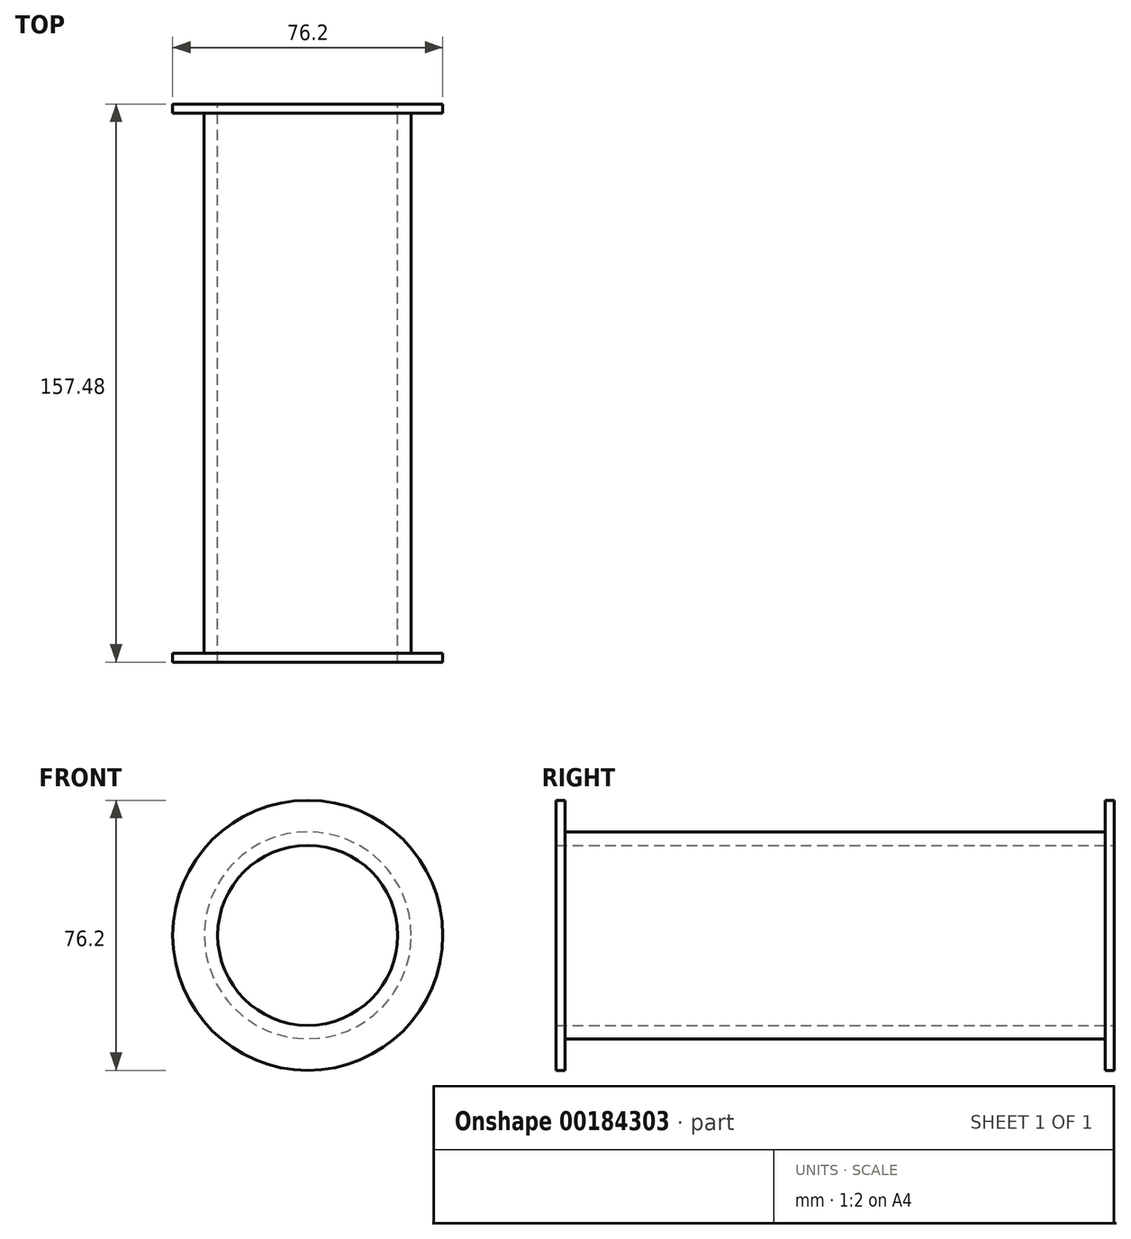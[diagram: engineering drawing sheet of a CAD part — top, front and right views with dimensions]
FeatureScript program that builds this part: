
annotation { "Feature Type Name" : "Feature", "Feature Type Description" : "" }
export const myFeature = defineFeature(function(context is Context, id is Id, definition is map)
    precondition{}
    {
        {
            var Q0;
            Q0=qCreatedBy(makeId("Front.planeOp"),FACE);
            var sketch = newSketch(context, id + "F0", { "sketchPlane" : qUnion([Q0])});
            skCircle(sketch, "E0", {"center": v(0, 0) * mm, "radius": 38.1 * mm});
            skCircle(sketch, "E1", {"center": v(0, 0) * mm, "radius": 25.4 * mm});
            skCircle(sketch, "E2", {"center": v(0, 0) * mm, "radius": 29.21 * mm});
            skSolve(sketch);
        }
        {
            var Q0;
            Q0=makeQuery(id+"F0.imprint","IMPRINT",FACE,{"disambiguationData":[TD([[makeQuery(id+"F0.imprint","IMPRINT",EDGE,{"derivedFrom":sQuery(id+"F0.wireOp",EDGE,"E0")}),1.0]])]});
            extrude(context, id + "F1", {"entities" : qUnion([Q0]), "depth" : 2.54 * mm});
        }
        {
            var Q0;
            Q0=makeQuery(id+"F0.imprint","IMPRINT",FACE,{"disambiguationData":[TD([[makeQuery(id+"F0.imprint","IMPRINT",EDGE,{"derivedFrom":sQuery(id+"F0.wireOp",EDGE,"E1")}),-1.0]])]});
            extrude(context, id + "F2", {"entities" : qUnion([Q0]), "operationType" : NewBodyOperationType.ADD, "depth" : 157.48 * mm});
        }
        {
            var Q0;
            Q0=makeQuery(id+"F2.opExtrude","CAP_FACE",FACE,{"disambiguationData":[OSD([sQuery(id+"F0.wireOp",EDGE,"E1"),sQuery(id+"F0.wireOp",EDGE,"E2")])],"isStart":false});
            var sketch = newSketch(context, id + "F3", { "sketchPlane" : qUnion([Q0])});
            skCircle(sketch, "E3", {"center": v(0, 0) * mm, "radius": 25.4 * mm});
            skCircle(sketch, "E4", {"center": v(0, 0) * mm, "radius": 38.1 * mm});
            skSolve(sketch);
        }
        {
            var Q0;
            Q0=makeQuery(id+"F3.imprint","IMPRINT",FACE,{"disambiguationData":[TD([[makeQuery(id+"F3.imprint","IMPRINT",EDGE,{"derivedFrom":sQuery(id+"F3.wireOp",EDGE,"E4")}),1.0]])]});
            extrude(context, id + "F4", {"entities" : qUnion([Q0]), "operationType" : NewBodyOperationType.ADD, "oppositeDirection" : true, "depth" : 2.54 * mm});
        }
    });
